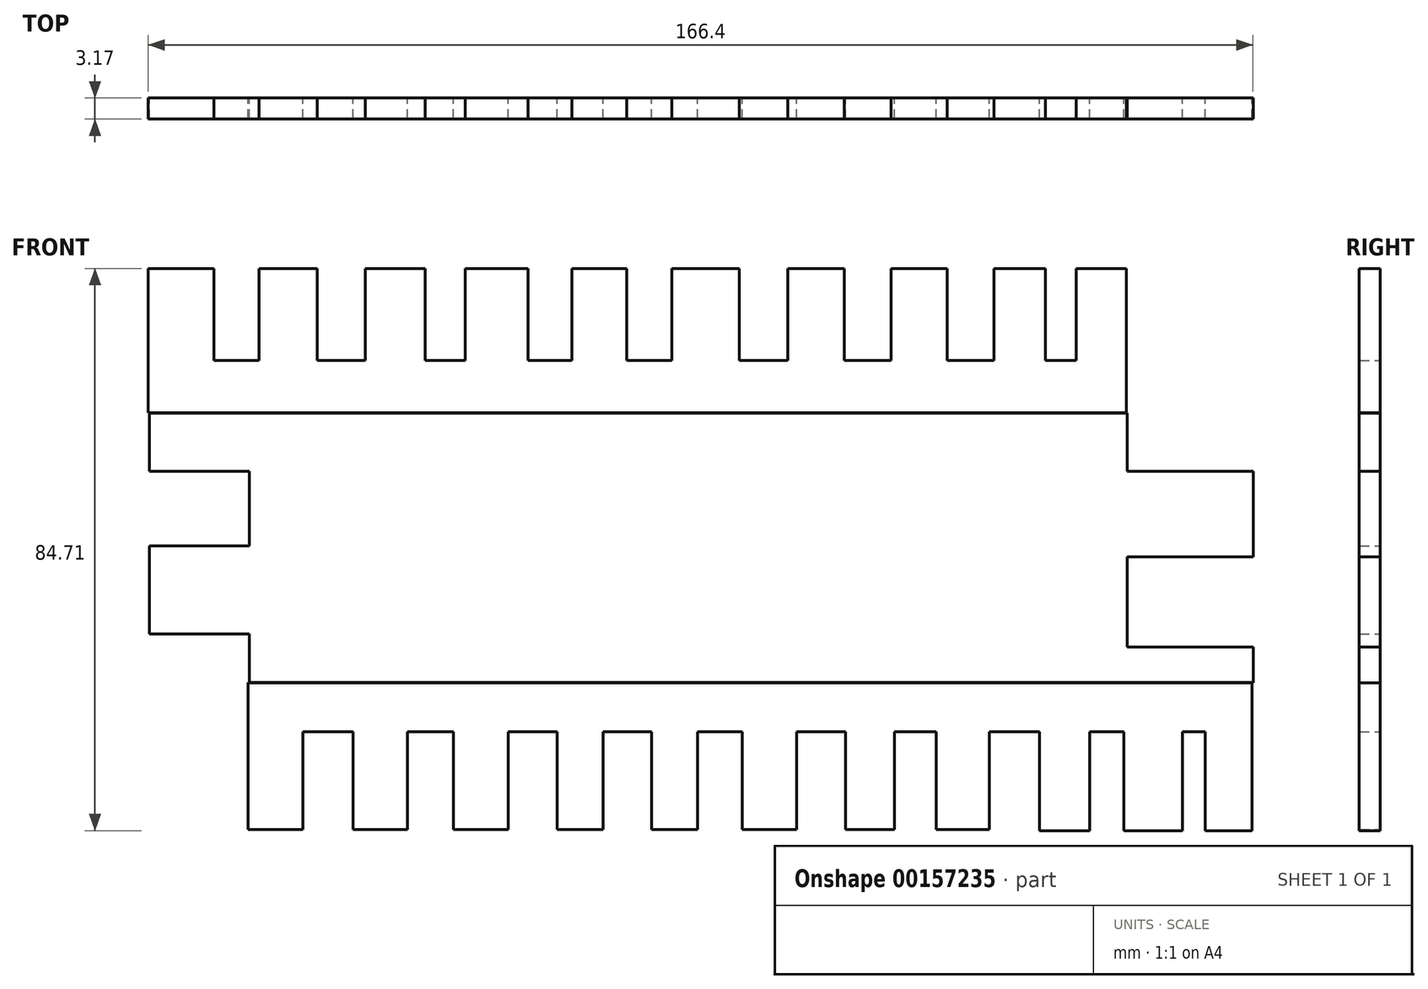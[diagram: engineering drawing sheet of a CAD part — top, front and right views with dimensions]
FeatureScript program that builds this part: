
annotation { "Feature Type Name" : "Feature", "Feature Type Description" : "" }
export const myFeature = defineFeature(function(context is Context, id is Id, definition is map)
    precondition{}
    {
        {
            var Q0;
            Q0=qCreatedBy(makeId("Front.planeOp"),FACE);
            var sketch = newSketch(context, id + "F0", { "sketchPlane" : qUnion([Q0])});
            skLineSegment(sketch, "E0", {"start": v(-69.83, 31.73) * mm, "end": v(77.47, 31.73) * mm});
            skLineSegment(sketch, "E1", {"start": v(-69.83, 31.73) * mm, "end": v(-69.83, 48.37) * mm});
            skLineSegment(sketch, "E2", {"start": v(-69.83, 31.73) * mm, "end": v(-69.83, 26.65) * mm});
            skLineSegment(sketch, "E3", {"start": v(77.47, 31.73) * mm, "end": v(77.47, 26.65) * mm});
            skLineSegment(sketch, "E4", {"start": v(-54.77, -19.07) * mm, "end": v(96.4, -19.07) * mm});
            skLineSegment(sketch, "E5", {"start": v(-54.77, -19.07) * mm, "end": v(-54.77, -36.16) * mm});
            skLineSegment(sketch, "E6", {"start": v(-54.77, -36.16) * mm, "end": v(-46.55, -36.16) * mm});
            skLineSegment(sketch, "E7", {"start": v(-46.55, -36.16) * mm, "end": v(-46.55, -21.44) * mm});
            skLineSegment(sketch, "E8", {"start": v(-46.55, -21.44) * mm, "end": v(-38.98, -21.44) * mm});
            skLineSegment(sketch, "E9", {"start": v(-38.98, -21.44) * mm, "end": v(-38.98, -36.16) * mm});
            skLineSegment(sketch, "E10", {"start": v(-38.98, -36.16) * mm, "end": v(-30.76, -36.16) * mm});
            skLineSegment(sketch, "E11", {"start": v(-30.76, -36.16) * mm, "end": v(-30.76, -21.44) * mm});
            skLineSegment(sketch, "E12", {"start": v(-30.76, -21.44) * mm, "end": v(-23.84, -21.44) * mm});
            skLineSegment(sketch, "E13", {"start": v(-23.84, -21.44) * mm, "end": v(-23.84, -36.16) * mm});
            skLineSegment(sketch, "E14", {"start": v(-23.84, -36.16) * mm, "end": v(-15.62, -36.16) * mm});
            skLineSegment(sketch, "E15", {"start": v(-15.62, -36.16) * mm, "end": v(-15.62, -21.44) * mm});
            skLineSegment(sketch, "E16", {"start": v(-15.62, -21.44) * mm, "end": v(-8.27, -21.44) * mm});
            skLineSegment(sketch, "E17", {"start": v(-8.27, -21.44) * mm, "end": v(-8.27, -36.16) * mm});
            skLineSegment(sketch, "E18", {"start": v(-8.27, -36.16) * mm, "end": v(-1.35, -36.16) * mm});
            skLineSegment(sketch, "E19", {"start": v(-1.35, -36.16) * mm, "end": v(-1.35, -21.44) * mm});
            skLineSegment(sketch, "E20", {"start": v(-1.35, -21.44) * mm, "end": v(6, -21.44) * mm});
            skLineSegment(sketch, "E21", {"start": v(6, -21.44) * mm, "end": v(6, -36.16) * mm});
            skLineSegment(sketch, "E22", {"start": v(6, -36.16) * mm, "end": v(12.93, -36.16) * mm});
            skLineSegment(sketch, "E23", {"start": v(12.93, -36.16) * mm, "end": v(12.93, -21.44) * mm});
            skLineSegment(sketch, "E24", {"start": v(12.93, -21.44) * mm, "end": v(19.63, -21.44) * mm});
            skLineSegment(sketch, "E25", {"start": v(19.63, -21.44) * mm, "end": v(19.63, -36.16) * mm});
            skLineSegment(sketch, "E26", {"start": v(19.63, -36.16) * mm, "end": v(27.85, -36.16) * mm});
            skLineSegment(sketch, "E27", {"start": v(27.85, -36.16) * mm, "end": v(27.85, -21.44) * mm});
            skLineSegment(sketch, "E28", {"start": v(27.85, -21.44) * mm, "end": v(35.2, -21.44) * mm});
            skLineSegment(sketch, "E29", {"start": v(35.2, -21.44) * mm, "end": v(35.2, -36.16) * mm});
            skLineSegment(sketch, "E30", {"start": v(35.2, -36.16) * mm, "end": v(42.56, -36.16) * mm});
            skLineSegment(sketch, "E31", {"start": v(42.56, -36.16) * mm, "end": v(42.56, -21.44) * mm});
            skLineSegment(sketch, "E32", {"start": v(42.56, -21.44) * mm, "end": v(48.83, -21.44) * mm});
            skLineSegment(sketch, "E33", {"start": v(48.83, -21.44) * mm, "end": v(48.83, -36.16) * mm});
            skLineSegment(sketch, "E34", {"start": v(48.83, -36.16) * mm, "end": v(56.83, -36.16) * mm});
            skLineSegment(sketch, "E35", {"start": v(56.83, -36.16) * mm, "end": v(56.83, -21.44) * mm});
            skLineSegment(sketch, "E36", {"start": v(56.83, -21.44) * mm, "end": v(64.4, -21.44) * mm});
            skLineSegment(sketch, "E37", {"start": v(64.4, -21.44) * mm, "end": v(64.4, -36.34) * mm});
            skLineSegment(sketch, "E38", {"start": v(64.4, -36.34) * mm, "end": v(71.97, -36.34) * mm});
            skLineSegment(sketch, "E39", {"start": v(71.97, -36.34) * mm, "end": v(71.97, -21.44) * mm});
            skLineSegment(sketch, "E40", {"start": v(71.97, -21.44) * mm, "end": v(77.13, -21.44) * mm});
            skLineSegment(sketch, "E41", {"start": v(77.13, -21.44) * mm, "end": v(77.13, -36.34) * mm});
            skLineSegment(sketch, "E42", {"start": v(96.4, -36.34) * mm, "end": v(96.4, -19.07) * mm});
            skLineSegment(sketch, "E43", {"start": v(-54.77, -13.99) * mm, "end": v(-54.77, -19.07) * mm});
            skLineSegment(sketch, "E44", {"start": v(96.4, -13.99) * mm, "end": v(96.4, -19.07) * mm});
            skPoint(sketch, "E45.endSnap0", {"position": v(-62.29, 17.88) * mm});
            skLineSegment(sketch, "E46", {"start": v(-69.83, 48.37) * mm, "end": v(-59.93, 48.37) * mm});
            skLineSegment(sketch, "E47", {"start": v(-59.93, 48.37) * mm, "end": v(-59.93, 34.54) * mm});
            skLineSegment(sketch, "E48", {"start": v(-59.93, 34.54) * mm, "end": v(-53.13, 34.54) * mm});
            skLineSegment(sketch, "E49", {"start": v(-53.13, 34.54) * mm, "end": v(-53.13, 48.37) * mm});
            skLineSegment(sketch, "E50", {"start": v(-53.13, 48.37) * mm, "end": v(-44.4, 48.37) * mm});
            skLineSegment(sketch, "E51", {"start": v(-44.4, 48.37) * mm, "end": v(-44.4, 34.54) * mm});
            skLineSegment(sketch, "E52", {"start": v(-44.4, 34.54) * mm, "end": v(-37.1, 34.54) * mm});
            skLineSegment(sketch, "E53", {"start": v(-37.1, 34.54) * mm, "end": v(-37.1, 48.37) * mm});
            skLineSegment(sketch, "E54", {"start": v(-37.1, 48.37) * mm, "end": v(-28.13, 48.37) * mm});
            skLineSegment(sketch, "E55", {"start": v(-28.13, 48.37) * mm, "end": v(-28.13, 34.54) * mm});
            skLineSegment(sketch, "E56", {"start": v(-28.13, 34.54) * mm, "end": v(-22.06, 34.54) * mm});
            skLineSegment(sketch, "E57", {"start": v(-22.06, 34.54) * mm, "end": v(-22.06, 48.37) * mm});
            skLineSegment(sketch, "E58", {"start": v(-22.06, 48.37) * mm, "end": v(-12.6, 48.37) * mm});
            skLineSegment(sketch, "E59", {"start": v(-12.6, 48.37) * mm, "end": v(-12.6, 34.54) * mm});
            skLineSegment(sketch, "E60", {"start": v(-12.6, 34.54) * mm, "end": v(-6.04, 34.54) * mm});
            skLineSegment(sketch, "E61", {"start": v(-6.04, 34.54) * mm, "end": v(-6.04, 48.37) * mm});
            skLineSegment(sketch, "E62", {"start": v(-6.04, 48.37) * mm, "end": v(2.21, 48.37) * mm});
            skLineSegment(sketch, "E63", {"start": v(2.21, 48.37) * mm, "end": v(2.21, 34.54) * mm});
            skLineSegment(sketch, "E64", {"start": v(2.21, 34.54) * mm, "end": v(9, 34.54) * mm});
            skLineSegment(sketch, "E65", {"start": v(9, 34.54) * mm, "end": v(9, 48.37) * mm});
            skLineSegment(sketch, "E66", {"start": v(9, 48.37) * mm, "end": v(19.2, 48.37) * mm});
            skLineSegment(sketch, "E67", {"start": v(19.2, 48.37) * mm, "end": v(19.2, 34.54) * mm});
            skLineSegment(sketch, "E68", {"start": v(19.2, 34.54) * mm, "end": v(26.49, 34.54) * mm});
            skLineSegment(sketch, "E69", {"start": v(26.49, 34.54) * mm, "end": v(26.49, 48.37) * mm});
            skLineSegment(sketch, "E70", {"start": v(26.49, 48.37) * mm, "end": v(34.98, 48.37) * mm});
            skLineSegment(sketch, "E71", {"start": v(34.98, 48.37) * mm, "end": v(34.98, 34.54) * mm});
            skLineSegment(sketch, "E72", {"start": v(34.98, 34.54) * mm, "end": v(42.02, 34.54) * mm});
            skLineSegment(sketch, "E73", {"start": v(42.02, 34.54) * mm, "end": v(42.02, 48.37) * mm});
            skLineSegment(sketch, "E74", {"start": v(42.02, 48.37) * mm, "end": v(50.52, 48.37) * mm});
            skLineSegment(sketch, "E75", {"start": v(50.52, 48.37) * mm, "end": v(50.52, 34.54) * mm});
            skLineSegment(sketch, "E76", {"start": v(50.52, 34.54) * mm, "end": v(57.56, 34.54) * mm});
            skLineSegment(sketch, "E77", {"start": v(57.56, 34.54) * mm, "end": v(57.56, 48.37) * mm});
            skLineSegment(sketch, "E78", {"start": v(57.56, 48.37) * mm, "end": v(65.32, 48.37) * mm});
            skLineSegment(sketch, "E79", {"start": v(65.32, 48.37) * mm, "end": v(65.32, 34.54) * mm});
            skLineSegment(sketch, "E80", {"start": v(65.32, 34.54) * mm, "end": v(69.94, 34.54) * mm});
            skLineSegment(sketch, "E81", {"start": v(69.94, 34.54) * mm, "end": v(69.94, 48.37) * mm});
            skLineSegment(sketch, "E82", {"start": v(69.94, 48.37) * mm, "end": v(77.47, 48.37) * mm});
            skLineSegment(sketch, "E83", {"start": v(77.47, 48.37) * mm, "end": v(77.47, 31.73) * mm});
            skLineSegment(sketch, "E84", {"start": v(77.13, -36.34) * mm, "end": v(85.94, -36.34) * mm});
            skLineSegment(sketch, "E85", {"start": v(85.94, -36.34) * mm, "end": v(85.94, -21.44) * mm});
            skLineSegment(sketch, "E86", {"start": v(85.94, -21.44) * mm, "end": v(89.34, -21.44) * mm});
            skLineSegment(sketch, "E87", {"start": v(89.34, -21.44) * mm, "end": v(89.34, -36.34) * mm});
            skLineSegment(sketch, "E88", {"start": v(89.34, -36.34) * mm, "end": v(96.4, -36.34) * mm});
            skLineSegment(sketch, "E89", {"start": v(-69.83, 26.65) * mm, "end": v(77.47, 26.65) * mm});
            skLineSegment(sketch, "E90", {"start": v(-54.77, -13.99) * mm, "end": v(96.4, -13.99) * mm});
            skSolve(sketch);
        }
        {
            var Q0;
            Q0 = qSketchRegion(id + "F0", true);
            extrude(context, id + "F1", {"entities" : qUnion([Q0]), "depth" : 3.17 * mm});
        }
        {
            var Q0;
            Q0=qCreatedBy(makeId("Front.planeOp"),FACE);
            var sketch = newSketch(context, id + "F2", { "sketchPlane" : qUnion([Q0])});
            skLineSegment(sketch, "E91", {"start": v(-69.67, 26.56) * mm, "end": v(-69.67, 17.79) * mm});
            skLineSegment(sketch, "E92", {"start": v(-69.67, 17.79) * mm, "end": v(-54.58, 17.79) * mm});
            skLineSegment(sketch, "E93", {"start": v(-54.58, 17.79) * mm, "end": v(-54.58, 6.59) * mm});
            skLineSegment(sketch, "E94", {"start": v(-54.58, 6.59) * mm, "end": v(-69.67, 6.59) * mm});
            skLineSegment(sketch, "E95", {"start": v(-69.67, 6.59) * mm, "end": v(-69.67, -6.7) * mm});
            skLineSegment(sketch, "E96", {"start": v(-69.67, -6.7) * mm, "end": v(-54.58, -6.7) * mm});
            skLineSegment(sketch, "E97", {"start": v(-54.58, -6.7) * mm, "end": v(-54.6, -14.08) * mm});
            skLineSegment(sketch, "E98", {"start": v(77.63, 26.56) * mm, "end": v(77.63, 17.79) * mm});
            skLineSegment(sketch, "E99", {"start": v(77.63, 17.79) * mm, "end": v(96.57, 17.79) * mm});
            skLineSegment(sketch, "E100", {"start": v(96.57, 17.79) * mm, "end": v(96.57, 4.9) * mm});
            skLineSegment(sketch, "E101", {"start": v(96.57, 4.9) * mm, "end": v(77.63, 4.9) * mm});
            skLineSegment(sketch, "E102", {"start": v(77.63, 4.9) * mm, "end": v(77.63, -8.67) * mm});
            skLineSegment(sketch, "E103", {"start": v(77.63, -8.67) * mm, "end": v(96.57, -8.67) * mm});
            skLineSegment(sketch, "E104", {"start": v(96.57, -8.67) * mm, "end": v(96.57, -14.08) * mm});
            skLineSegment(sketch, "E105", {"start": v(-69.67, 26.56) * mm, "end": v(77.63, 26.56) * mm});
            skLineSegment(sketch, "E106", {"start": v(-54.6, -14.08) * mm, "end": v(96.57, -14.08) * mm});
            skSolve(sketch);
        }
        {
            var Q0;
            Q0 = qSketchRegion(id + "F2", true);
            extrude(context, id + "F3", {"entities" : qUnion([Q0]), "depth" : 3.17 * mm});
        }
    });
